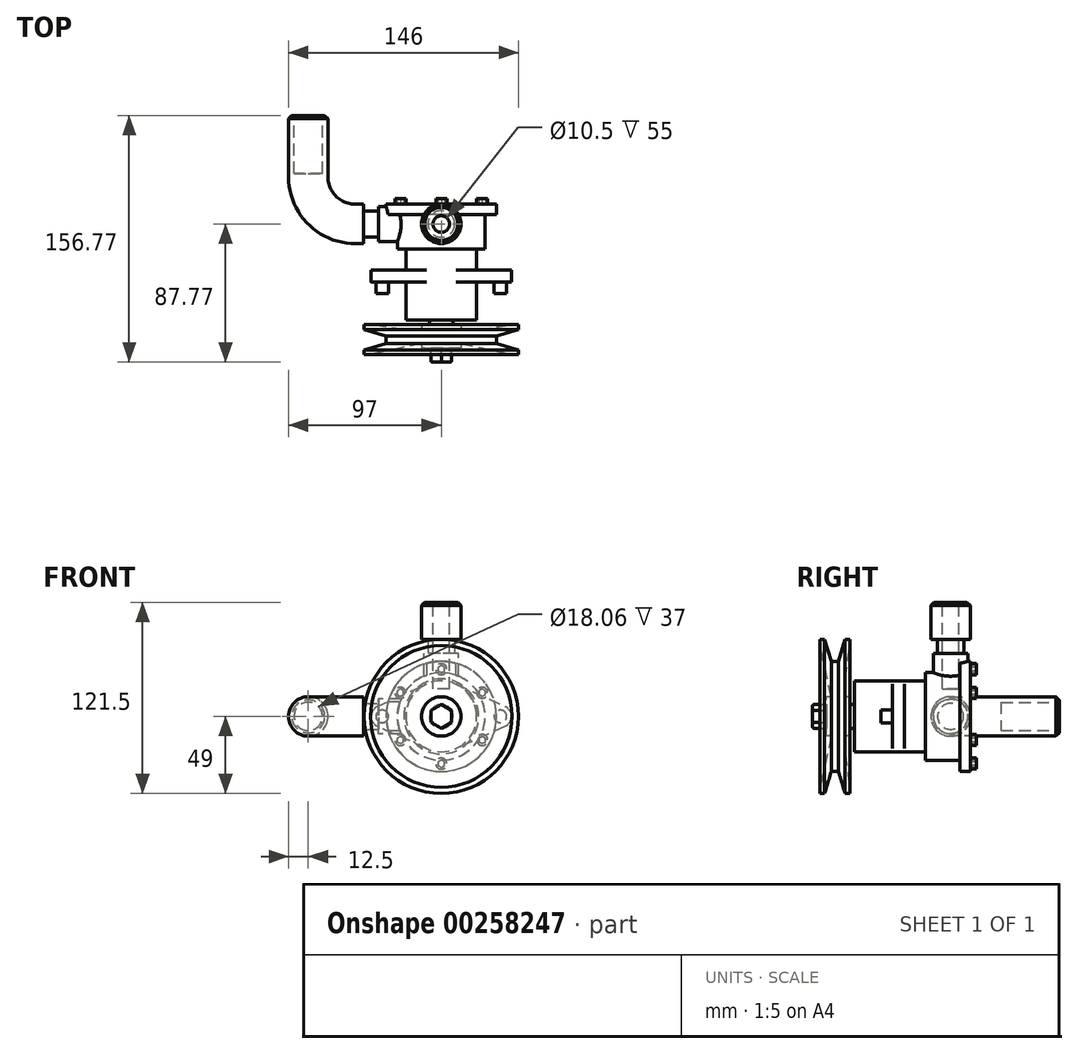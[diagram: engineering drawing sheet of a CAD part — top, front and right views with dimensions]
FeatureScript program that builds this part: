
annotation { "Feature Type Name" : "Feature", "Feature Type Description" : "" }
export const myFeature = defineFeature(function(context is Context, id is Id, definition is map)
    precondition{}
    {
        {
            var Q0;
            Q0=qCreatedBy(makeId("Front.planeOp"),FACE);
            var sketch = newSketch(context, id + "F0", { "sketchPlane" : qUnion([Q0])});
            skCircle(sketch, "E0", {"center": v(0, 0) * mm, "radius": 22.5 * mm});
            skSolve(sketch);
        }
        {
            var Q0;
            Q0 = qSketchRegion(id + "F0", true);
            extrude(context, id + "F1", {"entities" : qUnion([Q0]), "depth" : 24 * mm});
        }
        {
            var Q0;
            Q0 = qSketchRegion(id + "F0", true);
            extrude(context, id + "F2", {"entities" : qUnion([Q0]), "operationType" : NewBodyOperationType.ADD, "oppositeDirection" : true, "depth" : 21 * mm});
        }
        {
            var Q0;
            Q0=qCreatedBy(makeId("Front.planeOp"),FACE);
            var sketch = newSketch(context, id + "F3", { "sketchPlane" : qUnion([Q0])});
            skCircle(sketch, "E1", {"center": v(37.5, 0) * mm, "radius": 4 * mm});
            skCircle(sketch, "E2", {"center": v(-37.5, 0) * mm, "radius": 4 * mm});
            skLineSegment(sketch, "E3", {"start": v(-37.5, 0) * mm, "end": v(37.5, 0) * mm, "construction": true});
            skArc(sketch, "E4", {"start": v(-40.4, 6.37) * mm, "mid": v(-44.5, 0) * mm, "end": v(-40.4, -6.37) * mm});
            skArc(sketch, "E5", {"start": v(40.4, -6.37) * mm, "mid": v(44.5, 0) * mm, "end": v(40.4, 6.37) * mm});
            skLineSegment(sketch, "E6", {"start": v(-40.4, 6.37) * mm, "end": v(-9.3, 20.49) * mm});
            skLineSegment(sketch, "E7", {"start": v(9.3, 20.49) * mm, "end": v(40.4, 6.37) * mm});
            skLineSegment(sketch, "E8", {"start": v(40.4, -6.37) * mm, "end": v(9.3, -20.49) * mm});
            skLineSegment(sketch, "E9", {"start": v(-9.3, -20.49) * mm, "end": v(-40.4, -6.37) * mm});
            skArc(sketch, "E10.0", {"start": v(9.3, -20.49) * mm, "mid": v(22.5, 0) * mm, "end": v(9.3, 20.49) * mm});
            skArc(sketch, "E11.trimOffspring", {"start": v(-9.3, 20.49) * mm, "mid": v(-22.5, 0) * mm, "end": v(-9.3, -20.49) * mm});
            skSolve(sketch);
        }
        {
            var Q0;
            Q0 = qSketchRegion(id + "F3", true);
            extrude(context, id + "F4", {"entities" : qUnion([Q0]), "operationType" : NewBodyOperationType.ADD, "oppositeDirection" : true, "depth" : 7.8 * mm});
        }
        {
            var Q0;
            Q0=makeQuery(id+"F1.opExtrude","CAP_FACE",FACE,{"disambiguationData":[OSD([sQuery(id+"F0.wireOp",EDGE,"E0")])],"isStart":false});
            var sketch = newSketch(context, id + "F5", { "sketchPlane" : qUnion([Q0])});
            skCircle(sketch, "E12", {"center": v(0, 0) * mm, "radius": 7.5 * mm});
            skSolve(sketch);
        }
        {
            var Q0;
            Q0 = qSketchRegion(id + "F5", true);
            extrude(context, id + "F6", {"entities" : qUnion([Q0]), "operationType" : NewBodyOperationType.ADD, "depth" : 3 * mm});
        }
        {
            var Q0;
            Q0=qCreatedBy(makeId("Top.planeOp"),FACE);
            var sketch = newSketch(context, id + "F7", { "sketchPlane" : qUnion([Q0])});
            skLineSegment(sketch, "E13.0", {"start": v(7.5, -27) * mm, "end": v(-7.5, -27) * mm});
            skLineSegment(sketch, "E14", {"start": v(7.5, -27) * mm, "end": v(12.5, -27) * mm});
            skLineSegment(sketch, "E15", {"start": v(12.5, -27) * mm, "end": v(12.5, -30) * mm});
            skLineSegment(sketch, "E16", {"start": v(12.5, -30) * mm, "end": v(23.8, -30) * mm});
            skLineSegment(sketch, "E17", {"start": v(23.8, -30) * mm, "end": v(45, -27) * mm});
            skLineSegment(sketch, "E18", {"start": v(45, -27) * mm, "end": v(49, -27) * mm});
            skLineSegment(sketch, "E19", {"start": v(49, -27) * mm, "end": v(49, -30) * mm});
            skLineSegment(sketch, "E20", {"start": v(49, -30) * mm, "end": v(35, -34.2) * mm});
            skLineSegment(sketch, "E21", {"start": v(35, -34.2) * mm, "end": v(35, -38.8) * mm});
            skLineSegment(sketch, "E22", {"start": v(35, -38.8) * mm, "end": v(49, -43) * mm});
            skLineSegment(sketch, "E23", {"start": v(49, -43) * mm, "end": v(49, -46) * mm});
            skLineSegment(sketch, "E24", {"start": v(49, -46) * mm, "end": v(45, -46) * mm});
            skLineSegment(sketch, "E25", {"start": v(45, -46) * mm, "end": v(12.5, -38.8) * mm});
            skLineSegment(sketch, "E26", {"start": v(0, -38.8) * mm, "end": v(0, -27) * mm});
            skLineSegment(sketch, "E27", {"start": v(-23.78, -36.5) * mm, "end": v(35, -36.5) * mm, "construction": true});
            skLineSegment(sketch, "E28", {"start": v(12.5, -38.8) * mm, "end": v(12.5, -41.77) * mm});
            skLineSegment(sketch, "E29", {"start": v(12.5, -41.77) * mm, "end": v(0, -41.77) * mm});
            skLineSegment(sketch, "E30", {"start": v(0, -41.77) * mm, "end": v(0, -38.8) * mm});
            skSolve(sketch);
        }
        {
            var Q0;
            Q0 = qSketchRegion(id + "F7", true);
            var Q1;
            Q1=sQuery(id+"F7.wireOp",EDGE,"E26");
            revolve(context, id + "F8", {"operationType" : NewBodyOperationType.ADD, "entities" : qUnion([Q0]), "axis" : qUnion([Q1]), "revolveType" : RevolveType.FULL});
        }
        {
            var Q0;
            Q0=makeQuery(id+"F8.opRevolve","SWEPT_FACE",FACE,{"disambiguationData":[OSD([sQuery(id+"F7.wireOp",EDGE,"E29")])]});
            var sketch = newSketch(context, id + "F9", { "sketchPlane" : qUnion([Q0])});
            skCircle(sketch, "E31.cCircle", {"center": v(0, 0) * mm, "radius": 6.5 * mm, "construction": true});
            skLineSegment(sketch, "E31.0", {"start": v(6.5, 3.75) * mm, "end": v(6.5, -3.75) * mm});
            skLineSegment(sketch, "E31.1", {"start": v(6.5, -3.75) * mm, "end": v(0, -7.5) * mm});
            skLineSegment(sketch, "E31.2", {"start": v(0, -7.5) * mm, "end": v(-6.5, -3.75) * mm});
            skLineSegment(sketch, "E31.3", {"start": v(-6.5, -3.75) * mm, "end": v(-6.5, 3.75) * mm});
            skLineSegment(sketch, "E31.4", {"start": v(-6.5, 3.75) * mm, "end": v(0, 7.5) * mm});
            skLineSegment(sketch, "E31.5", {"start": v(0, 7.5) * mm, "end": v(6.5, 3.75) * mm});
            skPoint(sketch, "E31.0.midPoint", {"position": v(6.5, 0) * mm});
            skSolve(sketch);
        }
        {
            var Q0;
            Q0 = qSketchRegion(id + "F9", true);
            extrude(context, id + "F10", {"entities" : qUnion([Q0]), "operationType" : NewBodyOperationType.ADD, "depth" : 9 * mm});
        }
        {
            var Q0;
            Q0=makeQuery(id+"F10.opExtrude","CAP_FACE",FACE,{"disambiguationData":[OSD([sQuery(id+"F9.wireOp",EDGE,"E31.0"),sQuery(id+"F9.wireOp",EDGE,"E31.1"),sQuery(id+"F9.wireOp",EDGE,"E31.2"),sQuery(id+"F9.wireOp",EDGE,"E31.3"),sQuery(id+"F9.wireOp",EDGE,"E31.4"),sQuery(id+"F9.wireOp",EDGE,"E31.5")])],"isStart":false});
            fillet(context, id + "F11", {"entities" : qUnion([Q0]), "radius" : 1 * mm, "tangentPropagation" : true, "allowEdgeOverflow" : false});
        }
        {
            var Q0;
            Q0=makeQuery(id+"F2.opExtrude","CAP_FACE",FACE,{"disambiguationData":[OSD([sQuery(id+"F0.wireOp",EDGE,"E0")])],"isStart":false});
            var sketch = newSketch(context, id + "F12", { "sketchPlane" : qUnion([Q0])});
            skCircle(sketch, "E32", {"center": v(0, 0) * mm, "radius": 27.8 * mm});
            skSolve(sketch);
        }
        {
            var Q0;
            Q0 = qSketchRegion(id + "F12", true);
            extrude(context, id + "F13", {"entities" : qUnion([Q0]), "operationType" : NewBodyOperationType.ADD, "depth" : 22 * mm});
        }
        {
            var Q0;
            Q0=makeQuery(id+"F13.opExtrude","CAP_FACE",FACE,{"disambiguationData":[OSD([sQuery(id+"F12.wireOp",EDGE,"E32")])],"isStart":false});
            var sketch = newSketch(context, id + "F14", { "sketchPlane" : qUnion([Q0])});
            skCircle(sketch, "E33", {"center": v(0, 0) * mm, "radius": 35 * mm});
            skSolve(sketch);
        }
        {
            var Q0;
            Q0 = qSketchRegion(id + "F14", true);
            extrude(context, id + "F15", {"entities" : qUnion([Q0]), "operationType" : NewBodyOperationType.ADD, "depth" : 6.5 * mm});
        }
        {
            var Q0;
            Q0=makeQuery(id+"F15.opExtrude","CAP_FACE",FACE,{"disambiguationData":[OSD([sQuery(id+"F14.wireOp",EDGE,"E33")])],"isStart":false});
            var sketch = newSketch(context, id + "F16", { "sketchPlane" : qUnion([Q0])});
            skCircle(sketch, "E34", {"center": v(0, 30) * mm, "radius": 3.5 * mm});
            skCircle(sketch, "E35.cCircle", {"center": v(0, 30) * mm, "radius": 2 * mm, "construction": true});
            skLineSegment(sketch, "E35.0", {"start": v(2, 31.15) * mm, "end": v(2, 28.85) * mm});
            skLineSegment(sketch, "E35.1", {"start": v(2, 28.85) * mm, "end": v(0, 27.7) * mm});
            skLineSegment(sketch, "E35.2", {"start": v(0, 27.7) * mm, "end": v(-2, 28.85) * mm});
            skLineSegment(sketch, "E35.3", {"start": v(-2, 28.85) * mm, "end": v(-2, 31.15) * mm});
            skLineSegment(sketch, "E35.4", {"start": v(-2, 31.15) * mm, "end": v(0, 32.3) * mm});
            skLineSegment(sketch, "E35.5", {"start": v(0, 32.3) * mm, "end": v(2, 31.15) * mm});
            skPoint(sketch, "E35.0.midPoint", {"position": v(2, 30) * mm});
            skPoint(sketch, "E36.1.0", {"position": v(-24.98, 16.73) * mm});
            skCircle(sketch, "E36.1.1", {"center": v(-25.98, 15) * mm, "radius": 3.5 * mm});
            skCircle(sketch, "E36.1.2", {"center": v(-25.98, 15) * mm, "radius": 2 * mm, "construction": true});
            skLineSegment(sketch, "E36.1.3", {"start": v(-25.98, 17.3) * mm, "end": v(-23.98, 16.15) * mm});
            skLineSegment(sketch, "E36.1.4", {"start": v(-23.98, 16.15) * mm, "end": v(-23.98, 13.85) * mm});
            skLineSegment(sketch, "E36.1.5", {"start": v(-23.98, 13.85) * mm, "end": v(-25.98, 12.7) * mm});
            skLineSegment(sketch, "E36.1.6", {"start": v(-25.98, 12.7) * mm, "end": v(-27.98, 13.85) * mm});
            skLineSegment(sketch, "E36.1.7", {"start": v(-27.98, 13.85) * mm, "end": v(-27.98, 16.15) * mm});
            skLineSegment(sketch, "E36.1.8", {"start": v(-27.98, 16.15) * mm, "end": v(-25.98, 17.3) * mm});
            skPoint(sketch, "E36.2.0", {"position": v(-26.98, -13.27) * mm});
            skCircle(sketch, "E36.2.1", {"center": v(-25.98, -15) * mm, "radius": 3.5 * mm});
            skCircle(sketch, "E36.2.2", {"center": v(-25.98, -15) * mm, "radius": 2 * mm, "construction": true});
            skLineSegment(sketch, "E36.2.3", {"start": v(-27.98, -13.85) * mm, "end": v(-25.98, -12.7) * mm});
            skLineSegment(sketch, "E36.2.4", {"start": v(-25.98, -12.7) * mm, "end": v(-23.98, -13.85) * mm});
            skLineSegment(sketch, "E36.2.5", {"start": v(-23.98, -13.85) * mm, "end": v(-23.98, -16.15) * mm});
            skLineSegment(sketch, "E36.2.6", {"start": v(-23.98, -16.15) * mm, "end": v(-25.98, -17.3) * mm});
            skLineSegment(sketch, "E36.2.7", {"start": v(-25.98, -17.3) * mm, "end": v(-27.98, -16.15) * mm});
            skLineSegment(sketch, "E36.2.8", {"start": v(-27.98, -16.15) * mm, "end": v(-27.98, -13.85) * mm});
            skPoint(sketch, "E36.3.0", {"position": v(-2, -30) * mm});
            skCircle(sketch, "E36.3.1", {"center": v(0, -30) * mm, "radius": 3.5 * mm});
            skCircle(sketch, "E36.3.2", {"center": v(0, -30) * mm, "radius": 2 * mm, "construction": true});
            skLineSegment(sketch, "E36.3.3", {"start": v(-2, -31.15) * mm, "end": v(-2, -28.85) * mm});
            skLineSegment(sketch, "E36.3.4", {"start": v(-2, -28.85) * mm, "end": v(0, -27.7) * mm});
            skLineSegment(sketch, "E36.3.5", {"start": v(0, -27.7) * mm, "end": v(2, -28.85) * mm});
            skLineSegment(sketch, "E36.3.6", {"start": v(2, -28.85) * mm, "end": v(2, -31.15) * mm});
            skLineSegment(sketch, "E36.3.7", {"start": v(2, -31.15) * mm, "end": v(0, -32.3) * mm});
            skLineSegment(sketch, "E36.3.8", {"start": v(0, -32.3) * mm, "end": v(-2, -31.15) * mm});
            skPoint(sketch, "E36.4.0", {"position": v(24.98, -16.73) * mm});
            skCircle(sketch, "E36.4.1", {"center": v(25.98, -15) * mm, "radius": 3.5 * mm});
            skCircle(sketch, "E36.4.2", {"center": v(25.98, -15) * mm, "radius": 2 * mm, "construction": true});
            skLineSegment(sketch, "E36.4.3", {"start": v(25.98, -17.3) * mm, "end": v(23.98, -16.15) * mm});
            skLineSegment(sketch, "E36.4.4", {"start": v(23.98, -16.15) * mm, "end": v(23.98, -13.85) * mm});
            skLineSegment(sketch, "E36.4.5", {"start": v(23.98, -13.85) * mm, "end": v(25.98, -12.7) * mm});
            skLineSegment(sketch, "E36.4.6", {"start": v(25.98, -12.7) * mm, "end": v(27.98, -13.85) * mm});
            skLineSegment(sketch, "E36.4.7", {"start": v(27.98, -13.85) * mm, "end": v(27.98, -16.15) * mm});
            skLineSegment(sketch, "E36.4.8", {"start": v(27.98, -16.15) * mm, "end": v(25.98, -17.3) * mm});
            skPoint(sketch, "E36.5.0", {"position": v(26.98, 13.27) * mm});
            skCircle(sketch, "E36.5.1", {"center": v(25.98, 15) * mm, "radius": 3.5 * mm});
            skCircle(sketch, "E36.5.2", {"center": v(25.98, 15) * mm, "radius": 2 * mm, "construction": true});
            skLineSegment(sketch, "E36.5.3", {"start": v(27.98, 13.85) * mm, "end": v(25.98, 12.7) * mm});
            skLineSegment(sketch, "E36.5.4", {"start": v(25.98, 12.7) * mm, "end": v(23.98, 13.85) * mm});
            skLineSegment(sketch, "E36.5.5", {"start": v(23.98, 13.85) * mm, "end": v(23.98, 16.15) * mm});
            skLineSegment(sketch, "E36.5.6", {"start": v(23.98, 16.15) * mm, "end": v(25.98, 17.3) * mm});
            skLineSegment(sketch, "E36.5.7", {"start": v(25.98, 17.3) * mm, "end": v(27.98, 16.15) * mm});
            skLineSegment(sketch, "E36.5.8", {"start": v(27.98, 16.15) * mm, "end": v(27.98, 13.85) * mm});
            skPoint(sketch, "E36.center", {"position": v(0, 0) * mm});
            skSolve(sketch);
        }
        {
            var Q0;
            Q0 = qSketchRegion(id + "F16", true);
            extrude(context, id + "F17", {"entities" : qUnion([Q0]), "operationType" : NewBodyOperationType.ADD, "depth" : 3.8 * mm});
        }
        {
            var Q0;
            Q0=qCreatedBy(makeId("Right.planeOp"),FACE);
            cPlane(context, id + "F18", {"entities" : qUnion([Q0]), "cplaneType" : CPlaneType.OFFSET, "offset" : 40 * mm, "oppositeDirection" : true, "width" : 150 * mm, "height" : 150 * mm});
        }
        {
            var Q0;
            Q0=qCreatedBy(id+"F18.planeOp",FACE);
            var sketch = newSketch(context, id + "F19", { "sketchPlane" : qUnion([Q0])});
            skCircle(sketch, "E37", {"center": v(37, 0) * mm, "radius": 11 * mm});
            skSolve(sketch);
        }
        {
            var Q0;
            Q0 = qSketchRegion(id + "F19", true);
            extrude(context, id + "F20", {"entities" : qUnion([Q0]), "operationType" : NewBodyOperationType.ADD, "depth" : 25 * mm});
        }
        {
            var Q0;
            Q0=qCreatedBy(makeId("Top.planeOp"),FACE);
            cPlane(context, id + "F21", {"entities" : qUnion([Q0]), "cplaneType" : CPlaneType.OFFSET, "offset" : 40 * mm, "width" : 150 * mm, "height" : 150 * mm});
        }
        {
            var Q0;
            Q0=qCreatedBy(id+"F21.planeOp",FACE);
            var sketch = newSketch(context, id + "F22", { "sketchPlane" : qUnion([Q0])});
            skCircle(sketch, "E38", {"center": v(0, 37) * mm, "radius": 11 * mm});
            skSolve(sketch);
        }
        {
            var Q0;
            Q0 = qSketchRegion(id + "F22", true);
            extrude(context, id + "F23", {"entities" : qUnion([Q0]), "operationType" : NewBodyOperationType.ADD, "oppositeDirection" : true, "depth" : 25 * mm});
        }
        {
            var Q0;
            Q0=makeQuery(id+"F23.opExtrude","CAP_FACE",FACE,{"disambiguationData":[OSD([sQuery(id+"F22.wireOp",EDGE,"E38")])],"isStart":true});
            var sketch = newSketch(context, id + "F24", { "sketchPlane" : qUnion([Q0])});
            skCircle(sketch, "E39.0", {"center": v(0, 37) * mm, "radius": 8.5 * mm});
            skSolve(sketch);
        }
        {
            var Q0;
            Q0 = qSketchRegion(id + "F24", true);
            extrude(context, id + "F25", {"entities" : qUnion([Q0]), "operationType" : NewBodyOperationType.ADD, "depth" : 9 * mm});
        }
        {
            var Q0;
            Q0=makeQuery(id+"F25.opExtrude","CAP_FACE",FACE,{"disambiguationData":[OSD([sQuery(id+"F24.wireOp",EDGE,"E39.0")])],"isStart":false});
            var sketch = newSketch(context, id + "F26", { "sketchPlane" : qUnion([Q0])});
            skCircle(sketch, "E40", {"center": v(0, 37) * mm, "radius": 12.5 * mm});
            skSolve(sketch);
        }
        {
            var Q0;
            Q0 = qSketchRegion(id + "F26", true);
            extrude(context, id + "F27", {"entities" : qUnion([Q0]), "operationType" : NewBodyOperationType.ADD, "depth" : 23.5 * mm});
        }
        {
            var Q0;
            Q0=makeQuery(id+"F27.opExtrude","CAP_FACE",FACE,{"disambiguationData":[OSD([sQuery(id+"F26.wireOp",EDGE,"E40")])],"isStart":false});
            chamfer(context, id + "F28", {"entities" : qUnion([Q0]), "width" : 2 * mm, "tangentPropagation" : true});
        }
        {
            var Q0;
            Q0=makeQuery(id+"F27.opExtrude","CAP_FACE",FACE,{"disambiguationData":[OSD([sQuery(id+"F26.wireOp",EDGE,"E40")])],"isStart":false});
            var sketch = newSketch(context, id + "F29", { "sketchPlane" : qUnion([Q0])});
            skCircle(sketch, "E41", {"center": v(0, 37) * mm, "radius": 5.25 * mm});
            skSolve(sketch);
        }
        {
            var Q0;
            Q0 = qSketchRegion(id + "F29", true);
            extrude(context, id + "F30", {"entities" : qUnion([Q0]), "operationType" : NewBodyOperationType.REMOVE, "oppositeDirection" : true, "depth" : 55 * mm});
        }
        {
            var Q0;
            Q0=makeQuery(id+"F20.opExtrude","CAP_FACE",FACE,{"disambiguationData":[OSD([sQuery(id+"F19.wireOp",EDGE,"E37")])],"isStart":true});
            var sketch = newSketch(context, id + "F31", { "sketchPlane" : qUnion([Q0])});
            skCircle(sketch, "E42", {"center": v(-37, 0) * mm, "radius": 8.25 * mm});
            skSolve(sketch);
        }
        {
            var Q0;
            Q0 = qSketchRegion(id + "F31", true);
            extrude(context, id + "F32", {"entities" : qUnion([Q0]), "operationType" : NewBodyOperationType.ADD, "depth" : 9.5 * mm});
        }
        {
            var Q0;
            Q0=makeQuery(id+"F32.opExtrude","CAP_FACE",FACE,{"disambiguationData":[OSD([sQuery(id+"F31.wireOp",EDGE,"E42")])],"isStart":false});
            var sketch = newSketch(context, id + "F33", { "sketchPlane" : qUnion([Q0])});
            skCircle(sketch, "E43", {"center": v(-37, 0) * mm, "radius": 12.5 * mm});
            skSolve(sketch);
        }
        {
            var Q0;
            Q0=qCreatedBy(makeId("Top.planeOp"),FACE);
            var sketch = newSketch(context, id + "F34", { "sketchPlane" : qUnion([Q0])});
            skPoint(sketch, "E44.0", {"position": v(-49.5, 37) * mm});
            skLineSegment(sketch, "E45", {"start": v(-49.5, 37) * mm, "end": v(-54.5, 37) * mm});
            skArc(sketch, "E46", {"start": v(-54.5, 37) * mm, "mid": v(-75.71, 45.79) * mm, "end": v(-84.5, 67) * mm});
            skLineSegment(sketch, "E47", {"start": v(-84.5, 67) * mm, "end": v(-84.5, 106) * mm});
            skSolve(sketch);
        }
        {
            var Q0;
            Q0 = qSketchRegion(id + "F33", true);
            var Q1;
            Q1 = qConstructionFilter(qBodyType(qCreatedBy(id + "F34" ,EDGE), BodyType.WIRE), ConstructionObject.NO);
            sweep(context, id + "F35", {"operationType" : NewBodyOperationType.ADD, "profiles" : qUnion([Q0]), "path" : qUnion([Q1])});
        }
        {
            var Q0;
            Q0=makeQuery(id+"F35.opSweep","CAP_FACE",FACE,{"disambiguationData":[OSD([sQuery(id+"F33.wireOp",EDGE,"E43"),sQuery(id+"F34.wireOp",VERTEX,"E47.end")])],"isStart":false});
            chamfer(context, id + "F36", {"entities" : qUnion([Q0]), "width" : 2 * mm, "tangentPropagation" : true});
        }
        {
            var Q0;
            Q0=makeQuery(id+"F35.opSweep","CAP_FACE",FACE,{"disambiguationData":[OSD([sQuery(id+"F33.wireOp",EDGE,"E43"),sQuery(id+"F34.wireOp",VERTEX,"E47.end")])],"isStart":false});
            var sketch = newSketch(context, id + "F37", { "sketchPlane" : qUnion([Q0])});
            skCircle(sketch, "E48", {"center": v(84.5, 0) * mm, "radius": 9.03 * mm});
            skSolve(sketch);
        }
        {
            var Q0;
            Q0 = qSketchRegion(id + "F37", true);
            extrude(context, id + "F38", {"entities" : qUnion([Q0]), "operationType" : NewBodyOperationType.REMOVE, "oppositeDirection" : true, "depth" : 37 * mm});
        }
        {
            var Q0;
            Q0=makeQuery(id+"F4.opExtrude","CAP_FACE",FACE,{"disambiguationData":[OSD([sQuery(id+"F3.wireOp",EDGE,"E1"),sQuery(id+"F3.wireOp",EDGE,"E5"),sQuery(id+"F3.wireOp",EDGE,"E7"),sQuery(id+"F3.wireOp",EDGE,"E8"),sQuery(id+"F3.wireOp",EDGE,"E10.0")])],"isStart":false});
            var sketch = newSketch(context, id + "F39", { "sketchPlane" : qUnion([Q0])});
            skCircle(sketch, "E49.0", {"center": v(-37.5, 0) * mm, "radius": 4 * mm});
            skCircle(sketch, "E50.0", {"center": v(37.5, 0) * mm, "radius": 4 * mm});
            skSolve(sketch);
        }
        {
            var Q0;
            Q0 = qSketchRegion(id + "F39", true);
            extrude(context, id + "F40", {"entities" : qUnion([Q0]), "operationType" : NewBodyOperationType.ADD, "oppositeDirection" : true, "depth" : 15 * mm});
        }
    });
